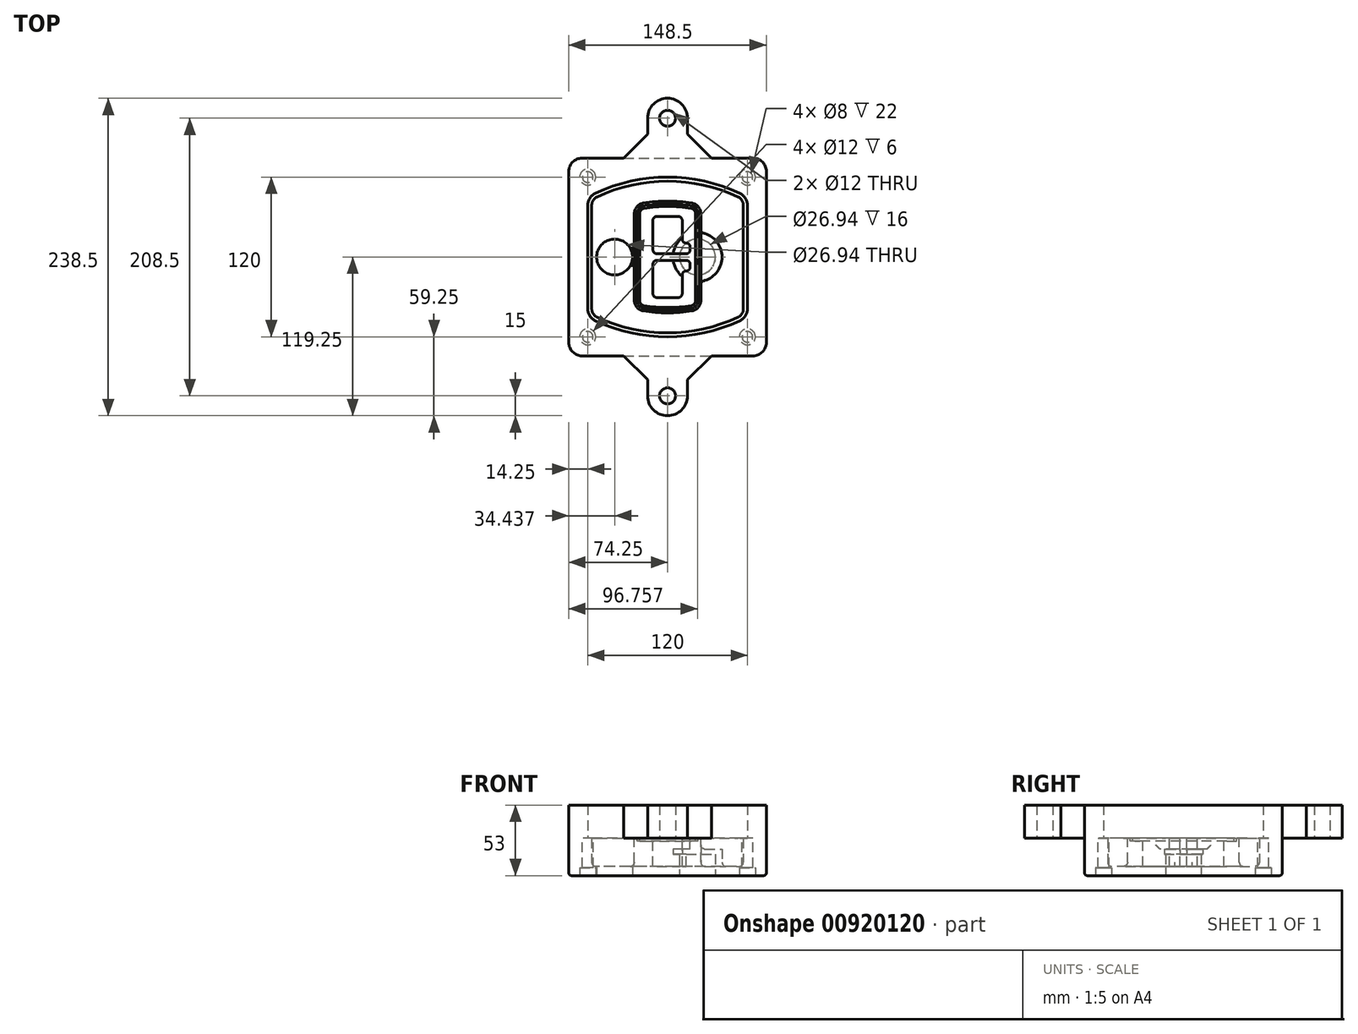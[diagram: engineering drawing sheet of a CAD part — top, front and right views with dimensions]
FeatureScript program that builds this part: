
annotation { "Feature Type Name" : "Feature", "Feature Type Description" : "" }
export const myFeature = defineFeature(function(context is Context, id is Id, definition is map)
    precondition{}
    {
        {
            var Q0;
            Q0=qCreatedBy(makeId("Top.planeOp"),FACE);
            var sketch = newSketch(context, id + "F0", { "sketchPlane" : qUnion([Q0])});
            skPoint(sketch, "E0.rect.middle", {"position": v(0, 0) * mm});
            skLineSegment(sketch, "E1.bottom", {"start": v(-64.25, -74.25) * mm, "end": v(64.25, -74.25) * mm});
            skLineSegment(sketch, "E1.top", {"start": v(-64.25, 74.25) * mm, "end": v(64.25, 74.25) * mm});
            skLineSegment(sketch, "E1.left", {"start": v(-74.25, -64.25) * mm, "end": v(-74.25, 64.25) * mm});
            skLineSegment(sketch, "E1.right", {"start": v(74.25, -64.25) * mm, "end": v(74.25, 64.25) * mm});
            skLineSegment(sketch, "E2", {"start": v(-74.25, 74.25) * mm, "end": v(74.25, -74.25) * mm, "construction": true});
            skLineSegment(sketch, "E3", {"start": v(74.25, 74.25) * mm, "end": v(-74.25, -74.25) * mm, "construction": true});
            skCircle(sketch, "E4", {"center": v(-60, 60) * mm, "radius": 4 * mm});
            skCircle(sketch, "E5", {"center": v(60, 60) * mm, "radius": 4 * mm});
            skCircle(sketch, "E6", {"center": v(60, -60) * mm, "radius": 4 * mm});
            skCircle(sketch, "E7", {"center": v(-60, -60) * mm, "radius": 4 * mm});
            skLineSegment(sketch, "E8", {"start": v(-60, 60) * mm, "end": v(60, 60) * mm, "construction": true});
            skLineSegment(sketch, "E9", {"start": v(60, 60) * mm, "end": v(60, -60) * mm, "construction": true});
            skLineSegment(sketch, "E10", {"start": v(60, -60) * mm, "end": v(-60, -60) * mm, "construction": true});
            skLineSegment(sketch, "E11", {"start": v(-60, -60) * mm, "end": v(-60, 60) * mm, "construction": true});
            skLineSegment(sketch, "E12", {"start": v(-60, 38.83) * mm, "end": v(-60, -38.83) * mm});
            skLineSegment(sketch, "E13", {"start": v(60, 38.83) * mm, "end": v(60, -38.83) * mm});
            skArc(sketch, "E14", {"start": v(54.26, 47.88) * mm, "mid": v(0, 60) * mm, "end": v(-54.26, 47.88) * mm});
            skArc(sketch, "E15", {"start": v(-54.26, -47.88) * mm, "mid": v(0, -60) * mm, "end": v(54.26, -47.88) * mm});
            skLineSegment(sketch, "E16", {"start": v(-60, 0) * mm, "end": v(60, 0) * mm, "construction": true});
            skPoint(sketch, "E17.visualSharp", {"position": v(-60, -45) * mm});
            skArc(sketch, "E17.filletArc", {"start": v(-60, -38.83) * mm, "mid": v(-58.44, -44.2) * mm, "end": v(-54.26, -47.88) * mm});
            skPoint(sketch, "E18.visualSharp", {"position": v(-60, 45) * mm});
            skArc(sketch, "E18.filletArc", {"start": v(-54.26, 47.88) * mm, "mid": v(-58.44, 44.2) * mm, "end": v(-60, 38.83) * mm});
            skPoint(sketch, "E19.visualSharp", {"position": v(60, 45) * mm});
            skArc(sketch, "E19.filletArc", {"start": v(60, 38.83) * mm, "mid": v(58.44, 44.2) * mm, "end": v(54.26, 47.88) * mm});
            skPoint(sketch, "E20.visualSharp", {"position": v(60, -45) * mm});
            skArc(sketch, "E20.filletArc", {"start": v(54.26, -47.88) * mm, "mid": v(58.44, -44.2) * mm, "end": v(60, -38.83) * mm});
            skPoint(sketch, "E21.visualSharp", {"position": v(-74.25, 74.25) * mm});
            skArc(sketch, "E21.filletArc", {"start": v(-64.25, 74.25) * mm, "mid": v(-71.32, 71.32) * mm, "end": v(-74.25, 64.25) * mm});
            skPoint(sketch, "E22.visualSharp", {"position": v(74.25, 74.25) * mm});
            skArc(sketch, "E22.filletArc", {"start": v(74.25, 64.25) * mm, "mid": v(71.32, 71.32) * mm, "end": v(64.25, 74.25) * mm});
            skPoint(sketch, "E23.visualSharp", {"position": v(74.25, -74.25) * mm});
            skArc(sketch, "E23.filletArc", {"start": v(64.25, -74.25) * mm, "mid": v(71.32, -71.32) * mm, "end": v(74.25, -64.25) * mm});
            skPoint(sketch, "E24.visualSharp", {"position": v(-74.25, -74.25) * mm});
            skArc(sketch, "E24.filletArc", {"start": v(-74.25, -64.25) * mm, "mid": v(-71.32, -71.32) * mm, "end": v(-64.25, -74.25) * mm});
            skArc(sketch, "E25.0", {"start": v(57, 38.83) * mm, "mid": v(55.9, 42.58) * mm, "end": v(52.98, 45.17) * mm});
            skLineSegment(sketch, "E25.1", {"start": v(57, 38.83) * mm, "end": v(57, -38.83) * mm});
            skArc(sketch, "E25.2", {"start": v(52.98, -45.17) * mm, "mid": v(55.9, -42.58) * mm, "end": v(57, -38.83) * mm});
            skArc(sketch, "E25.3", {"start": v(-52.98, -45.17) * mm, "mid": v(0, -57) * mm, "end": v(52.98, -45.17) * mm});
            skArc(sketch, "E25.4", {"start": v(-57, -38.83) * mm, "mid": v(-55.9, -42.58) * mm, "end": v(-52.98, -45.17) * mm});
            skArc(sketch, "E25.5", {"start": v(52.98, 45.17) * mm, "mid": v(0, 57) * mm, "end": v(-52.98, 45.17) * mm});
            skLineSegment(sketch, "E25.6", {"start": v(-57, 38.83) * mm, "end": v(-57, -38.83) * mm});
            skArc(sketch, "E25.7", {"start": v(-52.98, 45.17) * mm, "mid": v(-55.9, 42.58) * mm, "end": v(-57, 38.83) * mm});
            skArc(sketch, "E26.0", {"start": v(-55.96, 51.5) * mm, "mid": v(-61.82, 46.33) * mm, "end": v(-64, 38.83) * mm});
            skArc(sketch, "E26.1", {"start": v(55.96, 51.5) * mm, "mid": v(0, 64) * mm, "end": v(-55.96, 51.5) * mm});
            skArc(sketch, "E26.2", {"start": v(64, 38.83) * mm, "mid": v(61.82, 46.33) * mm, "end": v(55.96, 51.5) * mm});
            skLineSegment(sketch, "E26.3", {"start": v(64, 38.83) * mm, "end": v(64, -38.83) * mm});
            skArc(sketch, "E26.4", {"start": v(55.96, -51.5) * mm, "mid": v(61.82, -46.33) * mm, "end": v(64, -38.83) * mm});
            skLineSegment(sketch, "E26.5", {"start": v(-64, 38.83) * mm, "end": v(-64, -38.83) * mm});
            skArc(sketch, "E26.6", {"start": v(-55.96, -51.5) * mm, "mid": v(0, -64) * mm, "end": v(55.96, -51.5) * mm});
            skArc(sketch, "E26.7", {"start": v(-64, -38.83) * mm, "mid": v(-61.82, -46.33) * mm, "end": v(-55.96, -51.5) * mm});
            skSolve(sketch);
        }
        {
            var Q0;
            Q0=makeQuery(id+"F0.imprint","IMPRINT",FACE,{"disambiguationData":[TD([[makeQuery(id+"F0.imprint","IMPRINT",EDGE,{"derivedFrom":sQuery(id+"F0.wireOp",EDGE,"E1.bottom")}),1.0]])]});
            var Q1;
            Q1=makeQuery(id+"F0.imprint","IMPRINT",FACE,{"disambiguationData":[TD([[makeQuery(id+"F0.imprint","IMPRINT",EDGE,{"derivedFrom":sQuery(id+"F0.wireOp",EDGE,"E12")}),1.0]])]});
            var Q2;
            Q2=makeQuery(id+"F0.imprint","IMPRINT",FACE,{"disambiguationData":[TD([[makeQuery(id+"F0.imprint","IMPRINT",EDGE,{"derivedFrom":sQuery(id+"F0.wireOp",EDGE,"E25.0")}),1.0]])]});
            var Q3;
            Q3=makeQuery(id+"F0.imprint","IMPRINT",FACE,{"disambiguationData":[TD([[makeQuery(id+"F0.imprint","IMPRINT",EDGE,{"derivedFrom":sQuery(id+"F0.wireOp",EDGE,"E12")}),-1.0]])]});
            extrude(context, id + "F1", {"entities" : qUnion([Q0, Q1, Q2, Q3]), "oppositeDirection" : true, "depth" : 25 * mm});
        }
        {
            var Q0;
            Q0=makeQuery(id+"F0.imprint","IMPRINT",FACE,{"disambiguationData":[TD([[makeQuery(id+"F0.imprint","IMPRINT",EDGE,{"derivedFrom":sQuery(id+"F0.wireOp",EDGE,"E12")}),1.0]])]});
            extrude(context, id + "F2", {"entities" : qUnion([Q0]), "operationType" : NewBodyOperationType.ADD, "depth" : 3 * mm});
        }
        {
            var Q0;
            Q0=makeQuery(id+"F0.imprint","IMPRINT",FACE,{"disambiguationData":[TD([[makeQuery(id+"F0.imprint","IMPRINT",EDGE,{"derivedFrom":sQuery(id+"F0.wireOp",EDGE,"E25.0")}),1.0]])]});
            extrude(context, id + "F3", {"entities" : qUnion([Q0]), "operationType" : NewBodyOperationType.REMOVE, "oppositeDirection" : true, "depth" : 18 * mm});
        }
        {
            var Q0;
            Q0=makeQuery(id+"F2.opExtrude","CAP_FACE",FACE,{"disambiguationData":[OSD([sQuery(id+"F0.wireOp",EDGE,"E12"),sQuery(id+"F0.wireOp",EDGE,"E13"),sQuery(id+"F0.wireOp",EDGE,"E14"),sQuery(id+"F0.wireOp",EDGE,"E15"),sQuery(id+"F0.wireOp",EDGE,"E17.filletArc"),sQuery(id+"F0.wireOp",EDGE,"E18.filletArc"),sQuery(id+"F0.wireOp",EDGE,"E19.filletArc"),sQuery(id+"F0.wireOp",EDGE,"E20.filletArc"),sQuery(id+"F0.wireOp",EDGE,"E25.0"),sQuery(id+"F0.wireOp",EDGE,"E25.1"),sQuery(id+"F0.wireOp",EDGE,"E25.2"),sQuery(id+"F0.wireOp",EDGE,"E25.3"),sQuery(id+"F0.wireOp",EDGE,"E25.4"),sQuery(id+"F0.wireOp",EDGE,"E25.5"),sQuery(id+"F0.wireOp",EDGE,"E25.6"),sQuery(id+"F0.wireOp",EDGE,"E25.7")])],"isStart":false});
            var sketch = newSketch(context, id + "F4", { "sketchPlane" : qUnion([Q0])});
            skArc(sketch, "E27.0", {"start": v(-18.34, -40.45) * mm, "mid": v(0, -42) * mm, "end": v(18.34, -40.45) * mm});
            skArc(sketch, "E28.0", {"start": v(18.34, 40.45) * mm, "mid": v(0, 42) * mm, "end": v(-18.34, 40.45) * mm});
            skLineSegment(sketch, "E29", {"start": v(-25, 32.57) * mm, "end": v(-25, -32.57) * mm});
            skLineSegment(sketch, "E30", {"start": v(25, 32.57) * mm, "end": v(25, -32.57) * mm});
            skLineSegment(sketch, "E31", {"start": v(-25, 39.1) * mm, "end": v(25, 39.1) * mm, "construction": true});
            skLineSegment(sketch, "E32", {"start": v(-25, -39.1) * mm, "end": v(25, -39.1) * mm, "construction": true});
            skPoint(sketch, "E33.visualSharp", {"position": v(-25, 39.1) * mm});
            skArc(sketch, "E33.filletArc", {"start": v(-18.34, 40.45) * mm, "mid": v(-23.11, 37.73) * mm, "end": v(-25, 32.57) * mm});
            skPoint(sketch, "E34.visualSharp", {"position": v(25, 39.1) * mm});
            skArc(sketch, "E34.filletArc", {"start": v(25, 32.57) * mm, "mid": v(23.11, 37.73) * mm, "end": v(18.34, 40.45) * mm});
            skPoint(sketch, "E35.visualSharp", {"position": v(25, -39.1) * mm});
            skArc(sketch, "E35.filletArc", {"start": v(18.34, -40.45) * mm, "mid": v(23.11, -37.73) * mm, "end": v(25, -32.57) * mm});
            skPoint(sketch, "E36.visualSharp", {"position": v(-25, -39.1) * mm});
            skArc(sketch, "E36.filletArc", {"start": v(-25, -32.57) * mm, "mid": v(-23.11, -37.73) * mm, "end": v(-18.34, -40.45) * mm});
            skArc(sketch, "E37.0", {"start": v(52.98, 45.17) * mm, "mid": v(0, 57) * mm, "end": v(-52.98, 45.17) * mm});
            skArc(sketch, "E37.1", {"start": v(-52.98, 45.17) * mm, "mid": v(-55.9, 42.58) * mm, "end": v(-57, 38.83) * mm});
            skLineSegment(sketch, "E37.2", {"start": v(-57, 38.83) * mm, "end": v(-57, -38.83) * mm});
            skArc(sketch, "E37.3", {"start": v(-57, -38.83) * mm, "mid": v(-55.9, -42.58) * mm, "end": v(-52.98, -45.17) * mm});
            skArc(sketch, "E37.4", {"start": v(-52.98, -45.17) * mm, "mid": v(0, -57) * mm, "end": v(52.98, -45.17) * mm});
            skArc(sketch, "E37.5", {"start": v(52.98, -45.17) * mm, "mid": v(55.9, -42.58) * mm, "end": v(57, -38.83) * mm});
            skLineSegment(sketch, "E37.6", {"start": v(57, 38.83) * mm, "end": v(57, -38.83) * mm});
            skArc(sketch, "E37.7", {"start": v(57, 38.83) * mm, "mid": v(55.9, 42.58) * mm, "end": v(52.98, 45.17) * mm});
            skLineSegment(sketch, "E38.0", {"start": v(23, 32.57) * mm, "end": v(23, -32.57) * mm});
            skArc(sketch, "E38.1", {"start": v(18, -38.48) * mm, "mid": v(21.58, -36.44) * mm, "end": v(23, -32.57) * mm});
            skArc(sketch, "E38.2", {"start": v(-18, -38.48) * mm, "mid": v(0, -40) * mm, "end": v(18, -38.48) * mm});
            skArc(sketch, "E38.3", {"start": v(-23, -32.57) * mm, "mid": v(-21.58, -36.44) * mm, "end": v(-18, -38.48) * mm});
            skLineSegment(sketch, "E38.4", {"start": v(-23, 32.57) * mm, "end": v(-23, -32.57) * mm});
            skArc(sketch, "E38.5", {"start": v(23, 32.57) * mm, "mid": v(21.58, 36.44) * mm, "end": v(18, 38.48) * mm});
            skArc(sketch, "E38.6", {"start": v(-18, 38.48) * mm, "mid": v(-21.58, 36.44) * mm, "end": v(-23, 32.57) * mm});
            skArc(sketch, "E38.7", {"start": v(18, 38.48) * mm, "mid": v(0, 40) * mm, "end": v(-18, 38.48) * mm});
            skArc(sketch, "E39.0", {"start": v(21, 32.57) * mm, "mid": v(20.06, 35.15) * mm, "end": v(17.67, 36.5) * mm});
            skLineSegment(sketch, "E39.1", {"start": v(21, 32.57) * mm, "end": v(21, -32.57) * mm});
            skArc(sketch, "E39.2", {"start": v(17.67, -36.5) * mm, "mid": v(20.06, -35.15) * mm, "end": v(21, -32.57) * mm});
            skArc(sketch, "E39.3", {"start": v(-17.67, -36.5) * mm, "mid": v(0, -38) * mm, "end": v(17.67, -36.5) * mm});
            skArc(sketch, "E39.4", {"start": v(-21, -32.57) * mm, "mid": v(-20.06, -35.15) * mm, "end": v(-17.67, -36.5) * mm});
            skArc(sketch, "E39.5", {"start": v(17.67, 36.5) * mm, "mid": v(0, 38) * mm, "end": v(-17.67, 36.5) * mm});
            skLineSegment(sketch, "E39.6", {"start": v(-21, 32.57) * mm, "end": v(-21, -32.57) * mm});
            skArc(sketch, "E39.7", {"start": v(-17.67, 36.5) * mm, "mid": v(-20.06, 35.15) * mm, "end": v(-21, 32.57) * mm});
            skLineSegment(sketch, "E40", {"start": v(-25, 0) * mm, "end": v(25, 0) * mm, "construction": true});
            skLineSegment(sketch, "E41", {"start": v(-11, 5.5) * mm, "end": v(-11, 27.5) * mm});
            skLineSegment(sketch, "E42", {"start": v(-8, 30.5) * mm, "end": v(8, 30.5) * mm});
            skLineSegment(sketch, "E43", {"start": v(11, 27.5) * mm, "end": v(11, 13.5) * mm});
            skLineSegment(sketch, "E44", {"start": v(14, 10.5) * mm, "end": v(14, 10.5) * mm});
            skLineSegment(sketch, "E45", {"start": v(17, 7.5) * mm, "end": v(17, 5.5) * mm});
            skLineSegment(sketch, "E46", {"start": v(14, 2.5) * mm, "end": v(-8, 2.5) * mm});
            skPoint(sketch, "E47.visualSharp", {"position": v(-11, 30.5) * mm});
            skArc(sketch, "E47.filletArc", {"start": v(-8, 30.5) * mm, "mid": v(-10.12, 29.62) * mm, "end": v(-11, 27.5) * mm});
            skPoint(sketch, "E48.visualSharp", {"position": v(11, 30.5) * mm});
            skArc(sketch, "E48.filletArc", {"start": v(11, 27.5) * mm, "mid": v(10.12, 29.62) * mm, "end": v(8, 30.5) * mm});
            skPoint(sketch, "E49.visualSharp", {"position": v(11, 10.5) * mm});
            skArc(sketch, "E49.filletArc", {"start": v(11, 13.5) * mm, "mid": v(11.88, 11.38) * mm, "end": v(14, 10.5) * mm});
            skPoint(sketch, "E50.visualSharp", {"position": v(17, 10.5) * mm});
            skArc(sketch, "E50.filletArc", {"start": v(17, 7.5) * mm, "mid": v(16.12, 9.62) * mm, "end": v(14, 10.5) * mm});
            skPoint(sketch, "E51.visualSharp", {"position": v(17, 2.5) * mm});
            skArc(sketch, "E51.filletArc", {"start": v(14, 2.5) * mm, "mid": v(16.12, 3.38) * mm, "end": v(17, 5.5) * mm});
            skPoint(sketch, "E52.visualSharp", {"position": v(-11, 2.5) * mm});
            skArc(sketch, "E52.filletArc", {"start": v(-11, 5.5) * mm, "mid": v(-10.12, 3.38) * mm, "end": v(-8, 2.5) * mm});
            skLineSegment(sketch, "E53.0.MirrorCS", {"start": v(14, -2.5) * mm, "end": v(-8, -2.5) * mm});
            skArc(sketch, "E54.0.MirrorCS", {"start": v(-11, -5.5) * mm, "mid": v(-10.12, -3.38) * mm, "end": v(-8, -2.5) * mm});
            skLineSegment(sketch, "E55.0.MirrorCS", {"start": v(-11, -5.5) * mm, "end": v(-11, -27.5) * mm});
            skArc(sketch, "E56.0.MirrorCS", {"start": v(-8, -30.5) * mm, "mid": v(-10.12, -29.62) * mm, "end": v(-11, -27.5) * mm});
            skLineSegment(sketch, "E57.0.MirrorCS", {"start": v(-8, -30.5) * mm, "end": v(8, -30.5) * mm});
            skArc(sketch, "E58.0.MirrorCS", {"start": v(11, -27.5) * mm, "mid": v(10.12, -29.62) * mm, "end": v(8, -30.5) * mm});
            skLineSegment(sketch, "E59.0.MirrorCS", {"start": v(11, -27.5) * mm, "end": v(11, -13.5) * mm});
            skArc(sketch, "E60.0.MirrorCS", {"start": v(11, -13.5) * mm, "mid": v(11.88, -11.38) * mm, "end": v(14, -10.5) * mm});
            skArc(sketch, "E61.0.MirrorCS", {"start": v(17, -7.5) * mm, "mid": v(16.12, -9.62) * mm, "end": v(14, -10.5) * mm});
            skLineSegment(sketch, "E62.0.MirrorCS", {"start": v(17, -7.5) * mm, "end": v(17, -5.5) * mm});
            skArc(sketch, "E63.0.MirrorCS", {"start": v(14, -2.5) * mm, "mid": v(16.12, -3.38) * mm, "end": v(17, -5.5) * mm});
            skSolve(sketch);
        }
        {
            var Q0;
            Q0=makeQuery(id+"F4.imprint","IMPRINT",FACE,{"disambiguationData":[TD([[makeQuery(id+"F4.imprint","IMPRINT",EDGE,{"derivedFrom":sQuery(id+"F4.wireOp",EDGE,"E27.0")}),1.0]])]});
            var Q1;
            Q1=makeQuery(id+"F4.imprint","IMPRINT",FACE,{"disambiguationData":[TD([[makeQuery(id+"F4.imprint","IMPRINT",EDGE,{"derivedFrom":sQuery(id+"F4.wireOp",EDGE,"E38.0")}),-1.0]])]});
            var Q2;
            Q2=makeQuery(id+"F4.imprint","IMPRINT",FACE,{"disambiguationData":[TD([[makeQuery(id+"F4.imprint","IMPRINT",EDGE,{"derivedFrom":sQuery(id+"F4.wireOp",EDGE,"E39.0")}),1.0]])]});
            extrude(context, id + "F5", {"entities" : qUnion([Q0, Q1, Q2]), "operationType" : NewBodyOperationType.ADD, "endBound" : BoundingType.UP_TO_NEXT, "oppositeDirection" : true, "depth" : 25 * mm});
        }
        {
            var Q0;
            Q0=makeQuery(id+"F4.imprint","IMPRINT",FACE,{"disambiguationData":[TD([[makeQuery(id+"F4.imprint","IMPRINT",EDGE,{"derivedFrom":sQuery(id+"F4.wireOp",EDGE,"E38.0")}),-1.0]])]});
            extrude(context, id + "F6", {"entities" : qUnion([Q0]), "operationType" : NewBodyOperationType.REMOVE, "oppositeDirection" : true, "depth" : 2 * mm});
        }
        {
            var Q0;
            Q0=makeQuery(id+"F1.opExtrude","CAP_FACE",FACE,{"disambiguationData":[OSD([sQuery(id+"F0.wireOp",EDGE,"E1.bottom"),sQuery(id+"F0.wireOp",EDGE,"E1.top"),sQuery(id+"F0.wireOp",EDGE,"E1.left"),sQuery(id+"F0.wireOp",EDGE,"E1.right"),sQuery(id+"F0.wireOp",EDGE,"E4"),sQuery(id+"F0.wireOp",EDGE,"E5"),sQuery(id+"F0.wireOp",EDGE,"E6"),sQuery(id+"F0.wireOp",EDGE,"E7"),sQuery(id+"F0.wireOp",EDGE,"E21.filletArc"),sQuery(id+"F0.wireOp",EDGE,"E22.filletArc"),sQuery(id+"F0.wireOp",EDGE,"E23.filletArc"),sQuery(id+"F0.wireOp",EDGE,"E24.filletArc")])],"isStart":false});
            var sketch = newSketch(context, id + "F7", { "sketchPlane" : qUnion([Q0])});
            skCircle(sketch, "E64", {"center": v(22.5, 0) * mm, "radius": 13.47 * mm});
            skCircle(sketch, "E65", {"center": v(-39.81, 0) * mm, "radius": 13.47 * mm});
            skLineSegment(sketch, "E66", {"start": v(74.25, 0) * mm, "end": v(-74.25, 0) * mm});
            skCircle(sketch, "E67", {"center": v(22.5, 0) * mm, "radius": 18.47 * mm});
            skCircle(sketch, "E68", {"center": v(60, -60) * mm, "radius": 6 * mm});
            skCircle(sketch, "E69", {"center": v(-60, -60) * mm, "radius": 6 * mm});
            skCircle(sketch, "E70", {"center": v(-60, 60) * mm, "radius": 6 * mm});
            skCircle(sketch, "E71", {"center": v(60, 60) * mm, "radius": 6 * mm});
            skSolve(sketch);
        }
        {
            var Q0;
            {var subQ1=sQuery(id+"F7.wireOp",EDGE,"E66");var subQ4=sQuery(id+"F7.wireOp",EDGE,"E64");var subQ6=makeQuery(id+"F7.imprint","INTERSECT",VERTEX,{"disambiguationData":[OD(0.0)],"derivedFrom":[subQ4,subQ1]});Q0=makeQuery(id+"F7.imprint","IMPRINT",FACE,{"disambiguationData":[TD([[makeQuery(id+"F7.imprint","IMPRINT",EDGE,{"disambiguationData":[TD([[subQ6,-1.0]])],"derivedFrom":subQ4}),-1.0]])]});}
            var Q1;
            {var subQ0=sQuery(id+"F7.wireOp",EDGE,"E66");var subQ1=sQuery(id+"F7.wireOp",EDGE,"E64");var subQ3=makeQuery(id+"F7.imprint","INTERSECT",VERTEX,{"disambiguationData":[OD(0.0)],"derivedFrom":[subQ1,subQ0]});Q1=makeQuery(id+"F7.imprint","IMPRINT",FACE,{"disambiguationData":[TD([[makeQuery(id+"F7.imprint","IMPRINT",EDGE,{"disambiguationData":[TD([[subQ3,-1.0]])],"derivedFrom":subQ1}),1.0]])]});}
            var Q2;
            {var subQ0=sQuery(id+"F7.wireOp",EDGE,"E66");var subQ1=sQuery(id+"F7.wireOp",EDGE,"E64");var subQ3=makeQuery(id+"F7.imprint","INTERSECT",VERTEX,{"disambiguationData":[OD(0.0)],"derivedFrom":[subQ1,subQ0]});Q2=makeQuery(id+"F7.imprint","IMPRINT",FACE,{"disambiguationData":[TD([[makeQuery(id+"F7.imprint","IMPRINT",EDGE,{"disambiguationData":[TD([[subQ3,1.0]])],"derivedFrom":subQ1}),1.0]])]});}
            var Q3;
            {var subQ1=sQuery(id+"F7.wireOp",EDGE,"E66");var subQ4=sQuery(id+"F7.wireOp",EDGE,"E64");var subQ6=makeQuery(id+"F7.imprint","INTERSECT",VERTEX,{"disambiguationData":[OD(0.0)],"derivedFrom":[subQ4,subQ1]});Q3=makeQuery(id+"F7.imprint","IMPRINT",FACE,{"disambiguationData":[TD([[makeQuery(id+"F7.imprint","IMPRINT",EDGE,{"disambiguationData":[TD([[subQ6,1.0]])],"derivedFrom":subQ4}),-1.0]])]});}
            extrude(context, id + "F8", {"entities" : qUnion([Q0, Q1, Q2, Q3]), "operationType" : NewBodyOperationType.ADD, "oppositeDirection" : true, "depth" : 20 * mm});
        }
        {
            var Q0;
            {var subQ0=sQuery(id+"F7.wireOp",EDGE,"E66");var subQ1=sQuery(id+"F7.wireOp",EDGE,"E64");var subQ3=makeQuery(id+"F7.imprint","INTERSECT",VERTEX,{"disambiguationData":[OD(0.0)],"derivedFrom":[subQ1,subQ0]});Q0=makeQuery(id+"F7.imprint","IMPRINT",FACE,{"disambiguationData":[TD([[makeQuery(id+"F7.imprint","IMPRINT",EDGE,{"disambiguationData":[TD([[subQ3,-1.0]])],"derivedFrom":subQ1}),1.0]])]});}
            var Q1;
            {var subQ0=sQuery(id+"F7.wireOp",EDGE,"E66");var subQ1=sQuery(id+"F7.wireOp",EDGE,"E64");var subQ3=makeQuery(id+"F7.imprint","INTERSECT",VERTEX,{"disambiguationData":[OD(0.0)],"derivedFrom":[subQ1,subQ0]});Q1=makeQuery(id+"F7.imprint","IMPRINT",FACE,{"disambiguationData":[TD([[makeQuery(id+"F7.imprint","IMPRINT",EDGE,{"disambiguationData":[TD([[subQ3,1.0]])],"derivedFrom":subQ1}),1.0]])]});}
            extrude(context, id + "F9", {"entities" : qUnion([Q0, Q1]), "operationType" : NewBodyOperationType.REMOVE, "oppositeDirection" : true, "depth" : 16 * mm});
        }
        {
            var Q0;
            {var subQ0=sQuery(id+"F7.wireOp",EDGE,"E66");var subQ1=sQuery(id+"F7.wireOp",EDGE,"E65");var subQ3=makeQuery(id+"F7.imprint","INTERSECT",VERTEX,{"disambiguationData":[OD(0.0)],"derivedFrom":[subQ1,subQ0]});Q0=makeQuery(id+"F7.imprint","IMPRINT",FACE,{"disambiguationData":[TD([[makeQuery(id+"F7.imprint","IMPRINT",EDGE,{"disambiguationData":[TD([[subQ3,-1.0]])],"derivedFrom":subQ1}),1.0]])]});}
            var Q1;
            {var subQ0=sQuery(id+"F7.wireOp",EDGE,"E66");var subQ1=sQuery(id+"F7.wireOp",EDGE,"E65");var subQ3=makeQuery(id+"F7.imprint","INTERSECT",VERTEX,{"disambiguationData":[OD(0.0)],"derivedFrom":[subQ1,subQ0]});Q1=makeQuery(id+"F7.imprint","IMPRINT",FACE,{"disambiguationData":[TD([[makeQuery(id+"F7.imprint","IMPRINT",EDGE,{"disambiguationData":[TD([[subQ3,1.0]])],"derivedFrom":subQ1}),1.0]])]});}
            extrude(context, id + "F10", {"entities" : qUnion([Q0, Q1]), "operationType" : NewBodyOperationType.REMOVE, "oppositeDirection" : true, "depth" : 25 * mm});
        }
        {
            var Q0;
            Q0=makeQuery(id+"F7.imprint","IMPRINT",FACE,{"disambiguationData":[TD([[makeQuery(id+"F7.imprint","IMPRINT",EDGE,{"derivedFrom":sQuery(id+"F7.wireOp",EDGE,"E68")}),1.0]])]});
            var Q1;
            Q1=makeQuery(id+"F7.imprint","IMPRINT",FACE,{"disambiguationData":[TD([[makeQuery(id+"F7.imprint","IMPRINT",EDGE,{"derivedFrom":makeQuery(id+"F1.opExtrude","CAP_EDGE",EDGE,{"disambiguationData":[OSD([sQuery(id+"F0.wireOp",EDGE,"E5")])],"isStart":false})}),-1.0]])]});
            var Q2;
            Q2=makeQuery(id+"F7.imprint","IMPRINT",FACE,{"disambiguationData":[TD([[makeQuery(id+"F7.imprint","IMPRINT",EDGE,{"derivedFrom":sQuery(id+"F7.wireOp",EDGE,"E69")}),1.0]])]});
            var Q3;
            Q3=makeQuery(id+"F7.imprint","IMPRINT",FACE,{"disambiguationData":[TD([[makeQuery(id+"F7.imprint","IMPRINT",EDGE,{"derivedFrom":makeQuery(id+"F1.opExtrude","CAP_EDGE",EDGE,{"disambiguationData":[OSD([sQuery(id+"F0.wireOp",EDGE,"E4")])],"isStart":false})}),-1.0]])]});
            var Q4;
            Q4=makeQuery(id+"F7.imprint","IMPRINT",FACE,{"disambiguationData":[TD([[makeQuery(id+"F7.imprint","IMPRINT",EDGE,{"derivedFrom":sQuery(id+"F7.wireOp",EDGE,"E70")}),1.0]])]});
            var Q5;
            Q5=makeQuery(id+"F7.imprint","IMPRINT",FACE,{"disambiguationData":[TD([[makeQuery(id+"F7.imprint","IMPRINT",EDGE,{"derivedFrom":makeQuery(id+"F1.opExtrude","CAP_EDGE",EDGE,{"disambiguationData":[OSD([sQuery(id+"F0.wireOp",EDGE,"E7")])],"isStart":false})}),-1.0]])]});
            var Q6;
            Q6=makeQuery(id+"F7.imprint","IMPRINT",FACE,{"disambiguationData":[TD([[makeQuery(id+"F7.imprint","IMPRINT",EDGE,{"derivedFrom":sQuery(id+"F7.wireOp",EDGE,"E71")}),1.0]])]});
            var Q7;
            Q7=makeQuery(id+"F7.imprint","IMPRINT",FACE,{"disambiguationData":[TD([[makeQuery(id+"F7.imprint","IMPRINT",EDGE,{"derivedFrom":makeQuery(id+"F1.opExtrude","CAP_EDGE",EDGE,{"disambiguationData":[OSD([sQuery(id+"F0.wireOp",EDGE,"E6")])],"isStart":false})}),-1.0]])]});
            extrude(context, id + "F11", {"entities" : qUnion([Q0, Q1, Q2, Q3, Q4, Q5, Q6, Q7]), "operationType" : NewBodyOperationType.REMOVE, "oppositeDirection" : true, "depth" : 6 * mm});
        }
        {
            var Q0;
            Q0=makeQuery(id+"F9.boolean.opBoolean","COPY",FACE,{"derivedFrom":makeQuery(id+"F9.opExtrude","CAP_FACE",FACE,{"disambiguationData":[OSD([sQuery(id+"F7.wireOp",EDGE,"E64")])],"isStart":false})});
            var sketch = newSketch(context, id + "F12", { "sketchPlane" : qUnion([Q0])});
            skArc(sketch, "E72.0", {"start": v(11, 14.45) * mm, "mid": v(6.45, 9.13) * mm, "end": v(4.2, 2.5) * mm});
            skArc(sketch, "E72.1", {"start": v(4.2, -2.5) * mm, "mid": v(6.45, -9.13) * mm, "end": v(11, -14.45) * mm});
            skLineSegment(sketch, "E73", {"start": v(4.2, -2.5) * mm, "end": v(14, -2.5) * mm});
            skLineSegment(sketch, "E74.0", {"start": v(14, 2.5) * mm, "end": v(4.2, 2.5) * mm});
            skArc(sketch, "E74.1", {"start": v(14, 2.5) * mm, "mid": v(16.12, 3.38) * mm, "end": v(17, 5.5) * mm});
            skLineSegment(sketch, "E74.2", {"start": v(17, 7.5) * mm, "end": v(17, 5.5) * mm});
            skArc(sketch, "E74.3", {"start": v(17, 7.5) * mm, "mid": v(16.12, 9.62) * mm, "end": v(14, 10.5) * mm});
            skArc(sketch, "E74.4", {"start": v(11, 13.5) * mm, "mid": v(11.88, 11.38) * mm, "end": v(14, 10.5) * mm});
            skLineSegment(sketch, "E74.5", {"start": v(11, 14.45) * mm, "end": v(11, 13.5) * mm});
            skLineSegment(sketch, "E74.7", {"start": v(14, -2.5) * mm, "end": v(4.2, -2.5) * mm});
            skArc(sketch, "E74.8", {"start": v(14, -2.5) * mm, "mid": v(16.12, -3.38) * mm, "end": v(17, -5.5) * mm});
            skLineSegment(sketch, "E74.9", {"start": v(17, -7.5) * mm, "end": v(17, -5.5) * mm});
            skArc(sketch, "E74.10", {"start": v(17, -7.5) * mm, "mid": v(16.12, -9.62) * mm, "end": v(14, -10.5) * mm});
            skArc(sketch, "E74.11", {"start": v(11, -13.5) * mm, "mid": v(11.88, -11.38) * mm, "end": v(14, -10.5) * mm});
            skLineSegment(sketch, "E74.12", {"start": v(11, -14.45) * mm, "end": v(11, -13.5) * mm});
            skPoint(sketch, "E75.orphan", {"position": v(11, -27.5) * mm});
            skPoint(sketch, "E76.orphan", {"position": v(-8, -2.5) * mm});
            skPoint(sketch, "E77.orphan", {"position": v(-8, 2.5) * mm});
            skPoint(sketch, "E78.orphan", {"position": v(11, 27.5) * mm});
            skSolve(sketch);
        }
        {
            var Q0;
            {var subQ7=sQuery(id+"F12.wireOp",EDGE,"E72.0");var subQ14=sQuery(id+"F12.wireOp",EDGE,"E72.1");var subQ16=sQuery(id+"F12.wireOp",EDGE,"E74.1");var subQ18=sQuery(id+"F12.wireOp",EDGE,"E74.8");Q0=qUnion([makeQuery(id+"F12.imprint","IMPRINT",FACE,{"disambiguationData":[TD([[makeQuery(id+"F12.imprint","IMPRINT",EDGE,{"derivedFrom":subQ7}),1.0]])]}),makeQuery(id+"F12.imprint","IMPRINT",FACE,{"disambiguationData":[TD([[makeQuery(id+"F12.imprint","IMPRINT",EDGE,{"derivedFrom":subQ14}),1.0]])]}),makeQuery(id+"F12.imprint","IMPRINT",FACE,{"disambiguationData":[TD([[makeQuery(id+"F12.imprint","IMPRINT",EDGE,{"derivedFrom":subQ16}),1.0]])]}),makeQuery(id+"F12.imprint","IMPRINT",FACE,{"disambiguationData":[TD([[makeQuery(id+"F12.imprint","IMPRINT",EDGE,{"derivedFrom":subQ18}),-1.0]])]})]);}
            var Q1;
            Q1=makeQuery(id+"F5.boolean.opBoolean","SPLIT",FACE,{"disambiguationData":[TD([makeQuery(id+"F5.opExtrude","SWEPT_FACE",FACE,{"disambiguationData":[OSD([sQuery(id+"F4.wireOp",EDGE,"E41")])]})])],"derivedFrom":makeQuery(id+"F3.boolean.opBoolean","COPY",FACE,{"derivedFrom":makeQuery(id+"F3.opExtrude","CAP_FACE",FACE,{"disambiguationData":[OSD([sQuery(id+"F0.wireOp",EDGE,"E25.0"),sQuery(id+"F0.wireOp",EDGE,"E25.1"),sQuery(id+"F0.wireOp",EDGE,"E25.2"),sQuery(id+"F0.wireOp",EDGE,"E25.3"),sQuery(id+"F0.wireOp",EDGE,"E25.4"),sQuery(id+"F0.wireOp",EDGE,"E25.5"),sQuery(id+"F0.wireOp",EDGE,"E25.6"),sQuery(id+"F0.wireOp",EDGE,"E25.7")])],"isStart":false})})});
            extrude(context, id + "F13", {"entities" : qUnion([Q0]), "operationType" : NewBodyOperationType.REMOVE, "endBound" : BoundingType.UP_TO_SURFACE, "endBoundEntityFace" : qUnion([Q1]), "depth" : 25 * mm});
        }
        {
            var Q0;
            Q0=makeQuery(id+"F3.boolean.opBoolean","COPY",EDGE,{"derivedFrom":makeQuery(id+"F3.opExtrude","CAP_EDGE",EDGE,{"disambiguationData":[OSD([sQuery(id+"F0.wireOp",EDGE,"E25.6")])],"isStart":false})});
            var Q1;
            Q1=makeQuery(id+"F8.boolean.opBoolean","INTERSECT",EDGE,{"derivedFrom":[makeQuery(id+"F5.opExtrude","SWEPT_FACE",FACE,{"disambiguationData":[OSD([sQuery(id+"F4.wireOp",EDGE,"E30")])]}),makeQuery(id+"F8.opExtrude","CAP_FACE",FACE,{"disambiguationData":[OSD([sQuery(id+"F7.wireOp",EDGE,"E67")])],"isStart":false})]});
            var Q2;
            Q2=makeQuery(id+"F8.boolean.opBoolean","INTERSECT",EDGE,{"disambiguationData":[OD(1.0)],"derivedFrom":[makeQuery(id+"F5.opExtrude","SWEPT_FACE",FACE,{"disambiguationData":[OSD([sQuery(id+"F4.wireOp",EDGE,"E30")])]}),makeQuery(id+"F8.opExtrude","SWEPT_FACE",FACE,{"disambiguationData":[OSD([sQuery(id+"F7.wireOp",EDGE,"E67")])]})]});
            var Q3;
            {var subQ0=sQuery(id+"F4.wireOp",EDGE,"E30");Q3=makeQuery(id+"F8.boolean.opBoolean","SPLIT",EDGE,{"disambiguationData":[TD([makeQuery(id+"F5.opExtrude","SWEPT_FACE",FACE,{"disambiguationData":[OSD([sQuery(id+"F4.wireOp",EDGE,"E35.filletArc")])]})])],"derivedFrom":makeQuery(id+"F5.opExtrude","CAP_EDGE",EDGE,{"disambiguationData":[OSD([subQ0])],"isStart":false})});}
            var Q4;
            {var subQ0=sQuery(id+"F0.wireOp",EDGE,"E25.7");var subQ1=sQuery(id+"F0.wireOp",EDGE,"E25.1");var subQ2=sQuery(id+"F0.wireOp",EDGE,"E25.6");var subQ3=sQuery(id+"F0.wireOp",EDGE,"E25.5");var subQ4=sQuery(id+"F0.wireOp",EDGE,"E25.4");var subQ5=sQuery(id+"F0.wireOp",EDGE,"E25.0");var subQ6=sQuery(id+"F0.wireOp",EDGE,"E25.2");var subQ7=sQuery(id+"F0.wireOp",EDGE,"E25.3");Q4=makeQuery(id+"F8.boolean.opBoolean","INTERSECT",EDGE,{"derivedFrom":[makeQuery(id+"F5.boolean.opBoolean","SPLIT",FACE,{"disambiguationData":[TD([makeQuery(id+"F2.opExtrude","SWEPT_FACE",FACE,{"disambiguationData":[OSD([subQ5])]})])],"derivedFrom":makeQuery(id+"F3.boolean.opBoolean","COPY",FACE,{"derivedFrom":makeQuery(id+"F3.opExtrude","CAP_FACE",FACE,{"disambiguationData":[OSD([subQ5,subQ1,subQ6,subQ7,subQ4,subQ3,subQ2,subQ0])],"isStart":false})})}),makeQuery(id+"F8.opExtrude","SWEPT_FACE",FACE,{"disambiguationData":[OSD([sQuery(id+"F7.wireOp",EDGE,"E67")])]})]});}
            var Q5;
            Q5=makeQuery(id+"F8.boolean.opBoolean","INTERSECT",EDGE,{"disambiguationData":[OD(0.0)],"derivedFrom":[makeQuery(id+"F5.opExtrude","SWEPT_FACE",FACE,{"disambiguationData":[OSD([sQuery(id+"F4.wireOp",EDGE,"E30")])]}),makeQuery(id+"F8.opExtrude","SWEPT_FACE",FACE,{"disambiguationData":[OSD([sQuery(id+"F7.wireOp",EDGE,"E67")])]})]});
            fillet(context, id + "F14", {"entities" : qUnion([Q0, Q1, Q2, Q3, Q4, Q5]), "radius" : 3 * mm, "tangentPropagation" : true, "allowEdgeOverflow" : false});
        }
        {
            var Q0;
            Q0=makeQuery(id+"F1.opExtrude","CAP_EDGE",EDGE,{"disambiguationData":[OSD([sQuery(id+"F0.wireOp",EDGE,"E1.bottom")])],"isStart":false});
            fillet(context, id + "F15", {"entities" : qUnion([Q0]), "radius" : 2 * mm, "tangentPropagation" : true, "allowEdgeOverflow" : false});
        }
        {
            var Q0;
            {var subQ0=sQuery(id+"F0.wireOp",EDGE,"E21.filletArc");var subQ1=sQuery(id+"F0.wireOp",EDGE,"E7");var subQ2=sQuery(id+"F0.wireOp",EDGE,"E6");var subQ3=sQuery(id+"F0.wireOp",EDGE,"E5");var subQ4=sQuery(id+"F0.wireOp",EDGE,"E4");var subQ5=sQuery(id+"F0.wireOp",EDGE,"E22.filletArc");var subQ6=sQuery(id+"F0.wireOp",EDGE,"E1.bottom");var subQ7=sQuery(id+"F0.wireOp",EDGE,"E1.right");var subQ8=sQuery(id+"F0.wireOp",EDGE,"E1.top");var subQ9=sQuery(id+"F0.wireOp",EDGE,"E1.left");var subQ10=sQuery(id+"F0.wireOp",EDGE,"E23.filletArc");var subQ11=sQuery(id+"F0.wireOp",EDGE,"E24.filletArc");Q0=makeQuery(id+"F2.boolean.opBoolean","SPLIT",FACE,{"disambiguationData":[TD([makeQuery(id+"F1.opExtrude","SWEPT_FACE",FACE,{"disambiguationData":[OSD([subQ6])]})])],"derivedFrom":makeQuery(id+"F1.opExtrude","CAP_FACE",FACE,{"disambiguationData":[OSD([subQ6,subQ8,subQ9,subQ7,subQ4,subQ3,subQ2,subQ1,subQ0,subQ5,subQ10,subQ11])],"isStart":true})});}
            var sketch = newSketch(context, id + "F16", { "sketchPlane" : qUnion([Q0])});
            skCircle(sketch, "E79.0", {"center": v(-60, -60) * mm, "radius": 4 * mm});
            skCircle(sketch, "E79.1", {"center": v(60, -60) * mm, "radius": 4 * mm});
            skCircle(sketch, "E79.2", {"center": v(60, 60) * mm, "radius": 4 * mm});
            skCircle(sketch, "E79.3", {"center": v(-60, 60) * mm, "radius": 4 * mm});
            skLineSegment(sketch, "E80.0", {"start": v(-74.25, -64.25) * mm, "end": v(-74.25, 64.25) * mm});
            skLineSegment(sketch, "E81.0", {"start": v(-64.25, 74.25) * mm, "end": v(64.25, 74.25) * mm});
            skPoint(sketch, "E82.0", {"position": v(-71.32, 71.32) * mm});
            skArc(sketch, "E83.0", {"start": v(-64.25, 74.25) * mm, "mid": v(-71.32, 71.32) * mm, "end": v(-74.25, 64.25) * mm});
            skLineSegment(sketch, "E84.0.0", {"start": v(64.25, 74.25) * mm, "end": v(-64.25, 74.25) * mm});
            skLineSegment(sketch, "E84.0.2", {"start": v(-74.25, 64.25) * mm, "end": v(-74.25, -64.25) * mm});
            skArc(sketch, "E84.0.3", {"start": v(-74.25, -64.25) * mm, "mid": v(-71.32, -71.32) * mm, "end": v(-64.25, -74.25) * mm});
            skLineSegment(sketch, "E84.0.4", {"start": v(-64.25, -74.25) * mm, "end": v(64.25, -74.25) * mm});
            skArc(sketch, "E84.0.5", {"start": v(64.25, -74.25) * mm, "mid": v(71.32, -71.32) * mm, "end": v(74.25, -64.25) * mm});
            skLineSegment(sketch, "E84.0.6", {"start": v(74.25, -64.25) * mm, "end": v(74.25, 64.25) * mm});
            skArc(sketch, "E84.0.7", {"start": v(74.25, 64.25) * mm, "mid": v(71.32, 71.32) * mm, "end": v(64.25, 74.25) * mm});
            skLineSegment(sketch, "E85.0", {"start": v(-57, 38.83) * mm, "end": v(-57, -38.83) * mm});
            skLineSegment(sketch, "E86.0", {"start": v(-60, 38.83) * mm, "end": v(-60, -38.83) * mm});
            skArc(sketch, "E87.0", {"start": v(-60, -38.83) * mm, "mid": v(-58.44, -44.2) * mm, "end": v(-54.26, -47.88) * mm});
            skArc(sketch, "E88.0", {"start": v(-54.26, -47.88) * mm, "mid": v(0, -60) * mm, "end": v(54.26, -47.88) * mm});
            skArc(sketch, "E89.0", {"start": v(54.26, -47.88) * mm, "mid": v(58.44, -44.2) * mm, "end": v(60, -38.83) * mm});
            skLineSegment(sketch, "E90.0", {"start": v(60, 38.83) * mm, "end": v(60, -38.83) * mm});
            skArc(sketch, "E91.0", {"start": v(60, 38.83) * mm, "mid": v(58.44, 44.2) * mm, "end": v(54.26, 47.88) * mm});
            skArc(sketch, "E92.0", {"start": v(54.26, 47.88) * mm, "mid": v(0, 60) * mm, "end": v(-54.26, 47.88) * mm});
            skLineSegment(sketch, "E93.0.0", {"start": v(60, -38.83) * mm, "end": v(60, 38.83) * mm});
            skArc(sketch, "E93.0.3", {"start": v(-54.26, 47.88) * mm, "mid": v(-58.44, 44.2) * mm, "end": v(-60, 38.83) * mm});
            skSolve(sketch);
        }
        {
            var Q0;
            Q0 = qSketchRegion(id + "F16", true);
            var Q1;
            Q1=makeQuery(id+"F2.opExtrude","CAP_FACE",FACE,{"disambiguationData":[OSD([sQuery(id+"F0.wireOp",EDGE,"E12"),sQuery(id+"F0.wireOp",EDGE,"E13"),sQuery(id+"F0.wireOp",EDGE,"E14"),sQuery(id+"F0.wireOp",EDGE,"E15"),sQuery(id+"F0.wireOp",EDGE,"E17.filletArc"),sQuery(id+"F0.wireOp",EDGE,"E18.filletArc"),sQuery(id+"F0.wireOp",EDGE,"E19.filletArc"),sQuery(id+"F0.wireOp",EDGE,"E20.filletArc"),sQuery(id+"F0.wireOp",EDGE,"E25.0"),sQuery(id+"F0.wireOp",EDGE,"E25.1"),sQuery(id+"F0.wireOp",EDGE,"E25.2"),sQuery(id+"F0.wireOp",EDGE,"E25.3"),sQuery(id+"F0.wireOp",EDGE,"E25.4"),sQuery(id+"F0.wireOp",EDGE,"E25.5"),sQuery(id+"F0.wireOp",EDGE,"E25.6"),sQuery(id+"F0.wireOp",EDGE,"E25.7")])],"isStart":false});
            extrude(context, id + "F17", {"entities" : qUnion([Q0]), "endBound" : BoundingType.UP_TO_SURFACE, "depth" : 2 * mm, "endBoundEntityFace" : qUnion([Q1]), "offsetDistance" : 25 * mm});
        }
        {
            var Q0;
            Q0=makeQuery(id+"F17.opExtrude","CAP_FACE",FACE,{"disambiguationData":[OSD([sQuery(id+"F16.wireOp",EDGE,"E79.0"),sQuery(id+"F16.wireOp",EDGE,"E79.1"),sQuery(id+"F16.wireOp",EDGE,"E79.2"),sQuery(id+"F16.wireOp",EDGE,"E79.3"),sQuery(id+"F16.wireOp",EDGE,"E84.0.0"),sQuery(id+"F16.wireOp",EDGE,"E83.0"),sQuery(id+"F16.wireOp",EDGE,"E84.0.2"),sQuery(id+"F16.wireOp",EDGE,"E84.0.3"),sQuery(id+"F16.wireOp",EDGE,"E84.0.4"),sQuery(id+"F16.wireOp",EDGE,"E84.0.5"),sQuery(id+"F16.wireOp",EDGE,"E84.0.6"),sQuery(id+"F16.wireOp",EDGE,"E84.0.7"),sQuery(id+"F16.wireOp",EDGE,"E93.0.0"),sQuery(id+"F16.wireOp",EDGE,"E91.0"),sQuery(id+"F16.wireOp",EDGE,"E92.0"),sQuery(id+"F16.wireOp",EDGE,"E93.0.3"),sQuery(id+"F16.wireOp",EDGE,"E86.0"),sQuery(id+"F16.wireOp",EDGE,"E87.0"),sQuery(id+"F16.wireOp",EDGE,"E88.0"),sQuery(id+"F16.wireOp",EDGE,"E89.0")])],"isStart":false});
            var sketch = newSketch(context, id + "F18", { "sketchPlane" : qUnion([Q0])});
            skLineSegment(sketch, "E94", {"start": v(0, 74.25) * mm, "end": v(0, 104.25) * mm, "construction": true});
            skCircle(sketch, "E95", {"center": v(0, 104.25) * mm, "radius": 6 * mm});
            skArc(sketch, "E96", {"start": v(15, 104.25) * mm, "mid": v(0, 119.25) * mm, "end": v(-15, 104.25) * mm});
            skLineSegment(sketch, "E97", {"start": v(-15, 104.25) * mm, "end": v(-15, 92.25) * mm});
            skLineSegment(sketch, "E98", {"start": v(-15, 92.25) * mm, "end": v(-33, 74.25) * mm});
            skLineSegment(sketch, "E99.MirrorCS", {"start": v(15, 104.25) * mm, "end": v(15, 92.25) * mm});
            skLineSegment(sketch, "E100.MirrorCS", {"start": v(15, 92.25) * mm, "end": v(33, 74.25) * mm});
            skLineSegment(sketch, "E101.0.0", {"start": v(64.25, 74.25) * mm, "end": v(-64.25, 74.25) * mm});
            skArc(sketch, "E101.0.1", {"start": v(-64.25, 74.25) * mm, "mid": v(-71.32, 71.32) * mm, "end": v(-74.25, 64.25) * mm});
            skLineSegment(sketch, "E101.0.2", {"start": v(-74.25, 64.25) * mm, "end": v(-74.25, -64.25) * mm});
            skArc(sketch, "E101.0.3", {"start": v(-74.25, -64.25) * mm, "mid": v(-71.32, -71.32) * mm, "end": v(-64.25, -74.25) * mm});
            skLineSegment(sketch, "E101.0.4", {"start": v(-64.25, -74.25) * mm, "end": v(64.25, -74.25) * mm});
            skArc(sketch, "E101.0.5", {"start": v(64.25, -74.25) * mm, "mid": v(71.32, -71.32) * mm, "end": v(74.25, -64.25) * mm});
            skLineSegment(sketch, "E101.0.6", {"start": v(74.25, -64.25) * mm, "end": v(74.25, 64.25) * mm});
            skArc(sketch, "E101.0.7", {"start": v(74.25, 64.25) * mm, "mid": v(71.32, 71.32) * mm, "end": v(64.25, 74.25) * mm});
            skLineSegment(sketch, "E102", {"start": v(-74.25, 0) * mm, "end": v(74.25, 0) * mm, "construction": true});
            skLineSegment(sketch, "E103.MirrorCS", {"start": v(-15, -92.25) * mm, "end": v(-33, -74.25) * mm});
            skLineSegment(sketch, "E104.MirrorCS", {"start": v(-15, -104.25) * mm, "end": v(-15, -92.25) * mm});
            skArc(sketch, "E105.MirrorCS", {"start": v(15, -104.25) * mm, "mid": v(0, -119.25) * mm, "end": v(-15, -104.25) * mm});
            skCircle(sketch, "E106.MirrorC", {"center": v(0, -104.25) * mm, "radius": 6 * mm});
            skLineSegment(sketch, "E107.MirrorCS", {"start": v(15, -104.25) * mm, "end": v(15, -92.25) * mm});
            skLineSegment(sketch, "E108.MirrorCS", {"start": v(15, -92.25) * mm, "end": v(33, -74.25) * mm});
            skLineSegment(sketch, "E109.MirrorCS", {"start": v(0, -74.25) * mm, "end": v(0, -104.25) * mm, "construction": true});
            skSolve(sketch);
        }
        {
            var Q0;
            Q0=makeQuery(id+"F18.imprint","IMPRINT",FACE,{"disambiguationData":[TD([[makeQuery(id+"F18.imprint","IMPRINT",EDGE,{"derivedFrom":makeQuery(id+"F17.opExtrude","CAP_EDGE",EDGE,{"disambiguationData":[OSD([sQuery(id+"F16.wireOp",EDGE,"E79.0")])],"isStart":false})}),1.0]])]});
            var Q1;
            Q1=makeQuery(id+"F18.imprint","IMPRINT",FACE,{"disambiguationData":[TD([[makeQuery(id+"F18.imprint","IMPRINT",EDGE,{"derivedFrom":makeQuery(id+"F17.opExtrude","CAP_EDGE",EDGE,{"disambiguationData":[OSD([sQuery(id+"F16.wireOp",EDGE,"E79.1")])],"isStart":false})}),1.0]])]});
            var Q2;
            Q2=makeQuery(id+"F18.imprint","IMPRINT",FACE,{"disambiguationData":[TD([[makeQuery(id+"F18.imprint","IMPRINT",EDGE,{"derivedFrom":makeQuery(id+"F17.opExtrude","CAP_EDGE",EDGE,{"disambiguationData":[OSD([sQuery(id+"F16.wireOp",EDGE,"E79.2")])],"isStart":false})}),1.0]])]});
            var Q3;
            Q3=makeQuery(id+"F18.imprint","IMPRINT",FACE,{"disambiguationData":[TD([[makeQuery(id+"F18.imprint","IMPRINT",EDGE,{"derivedFrom":makeQuery(id+"F17.opExtrude","CAP_EDGE",EDGE,{"disambiguationData":[OSD([sQuery(id+"F16.wireOp",EDGE,"E79.3")])],"isStart":false})}),1.0]])]});
            var Q4;
            Q4=makeQuery(id+"F18.imprint","IMPRINT",FACE,{"disambiguationData":[TD([[makeQuery(id+"F18.imprint","IMPRINT",EDGE,{"derivedFrom":sQuery(id+"F18.wireOp",EDGE,"E95")}),-1.0]])]});
            var Q5;
            {var subQ0=sQuery(id+"F18.wireOp",EDGE,"E103.MirrorCS");Q5=makeQuery(id+"F18.imprint","IMPRINT",FACE,{"disambiguationData":[TD([[makeQuery(id+"F18.imprint","IMPRINT",EDGE,{"derivedFrom":subQ0}),-1.0]])]});}
            var Q6;
            {var subQ1=sQuery(id+"F18.wireOp",EDGE,"E101.0.1");Q6=makeQuery(id+"F18.imprint","IMPRINT",FACE,{"disambiguationData":[TD([[makeQuery(id+"F18.imprint","IMPRINT",EDGE,{"derivedFrom":subQ1}),1.0]])]});}
            extrude(context, id + "F19", {"entities" : qUnion([Q0, Q1, Q2, Q3, Q4, Q5, Q6]), "operationType" : NewBodyOperationType.ADD, "depth" : 25 * mm, "offsetDistance" : 25 * mm});
        }
    });
